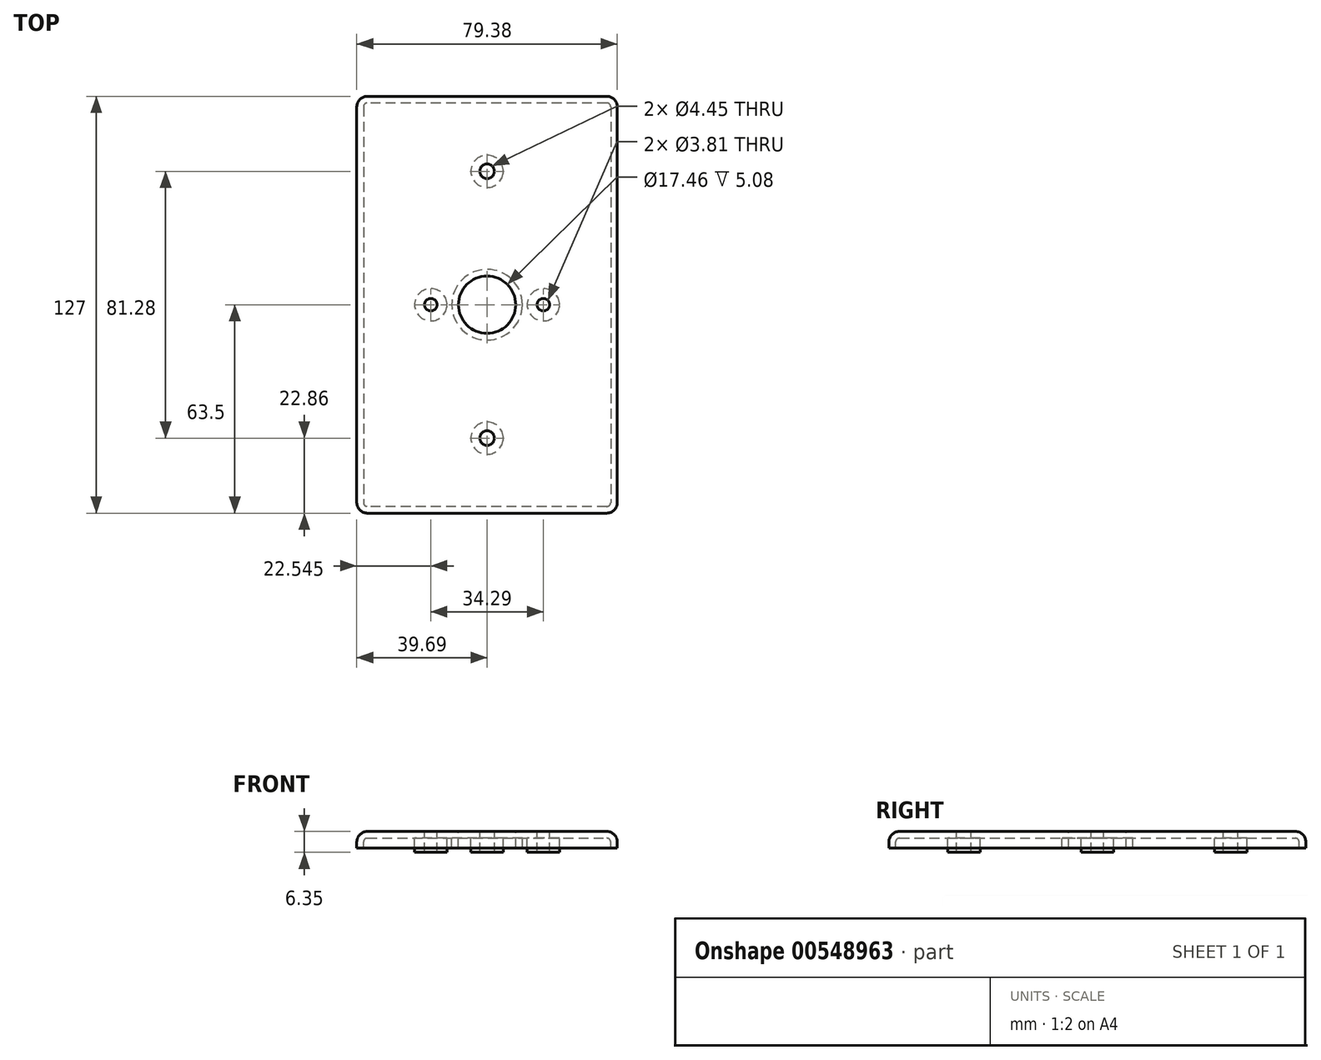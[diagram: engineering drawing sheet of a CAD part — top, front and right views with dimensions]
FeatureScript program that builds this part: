
annotation { "Feature Type Name" : "Feature", "Feature Type Description" : "" }
export const myFeature = defineFeature(function(context is Context, id is Id, definition is map)
    precondition{}
    {
        {
            var Q0;
            Q0=qCreatedBy(makeId("Top.planeOp"),FACE);
            var sketch = newSketch(context, id + "F0", { "sketchPlane" : qUnion([Q0])});
            skLineSegment(sketch, "E0.bottom", {"start": v(36.51, 63.5) * mm, "end": v(-36.51, 63.5) * mm});
            skLineSegment(sketch, "E0.top", {"start": v(36.51, -63.5) * mm, "end": v(-36.51, -63.5) * mm});
            skLineSegment(sketch, "E0.left", {"start": v(39.69, 60.33) * mm, "end": v(39.69, -60.33) * mm});
            skLineSegment(sketch, "E0.right", {"start": v(-39.69, 60.33) * mm, "end": v(-39.69, -60.33) * mm});
            skPoint(sketch, "E0.middle", {"position": v(0, 0) * mm});
            skCircle(sketch, "E1", {"center": v(0, 40.64) * mm, "radius": 2.22 * mm});
            skCircle(sketch, "E2", {"center": v(0, -40.64) * mm, "radius": 2.22 * mm});
            skCircle(sketch, "E3", {"center": v(-17.14, 0) * mm, "radius": 1.9 * mm});
            skCircle(sketch, "E4", {"center": v(17.15, 0) * mm, "radius": 1.9 * mm});
            skPoint(sketch, "E5.visualSharp", {"position": v(-39.69, 63.5) * mm});
            skArc(sketch, "E5.filletArc", {"start": v(-36.51, 63.5) * mm, "mid": v(-38.76, 62.57) * mm, "end": v(-39.69, 60.33) * mm});
            skPoint(sketch, "E6.visualSharp", {"position": v(39.69, 63.5) * mm});
            skArc(sketch, "E6.filletArc", {"start": v(39.69, 60.33) * mm, "mid": v(38.76, 62.57) * mm, "end": v(36.51, 63.5) * mm});
            skPoint(sketch, "E7.visualSharp", {"position": v(39.69, -63.5) * mm});
            skArc(sketch, "E7.filletArc", {"start": v(36.51, -63.5) * mm, "mid": v(38.76, -62.57) * mm, "end": v(39.69, -60.33) * mm});
            skPoint(sketch, "E8.visualSharp", {"position": v(-39.69, -63.5) * mm});
            skArc(sketch, "E8.filletArc", {"start": v(-39.69, -60.33) * mm, "mid": v(-38.76, -62.57) * mm, "end": v(-36.51, -63.5) * mm});
            skCircle(sketch, "E9", {"center": v(0, 0) * mm, "radius": 8.73 * mm});
            skSolve(sketch);
        }
        {
            var Q0;
            Q0=makeQuery(id+"F0.imprint","IMPRINT",FACE,{"disambiguationData":[TD([[makeQuery(id+"F0.imprint","IMPRINT",EDGE,{"derivedFrom":sQuery(id+"F0.wireOp",EDGE,"E0.bottom")}),1.0]])]});
            extrude(context, id + "F1", {"entities" : qUnion([Q0]), "oppositeDirection" : true, "depth" : 5.08 * mm, "offsetDistance" : 25.4 * mm});
        }
        {
            var Q0;
            Q0=makeQuery(id+"F1.opExtrude","CAP_EDGE",EDGE,{"disambiguationData":[OSD([sQuery(id+"F0.wireOp",EDGE,"E0.top")])],"isStart":true});
            fillet(context, id + "F2", {"entities" : qUnion([Q0]), "radius" : 3.17 * mm, "tangentPropagation" : true, "allowEdgeOverflow" : false});
        }
        {
            var Q0;
            Q0=makeQuery(id+"F1.opExtrude","CAP_FACE",FACE,{"disambiguationData":[OSD([sQuery(id+"F0.wireOp",EDGE,"E0.bottom"),sQuery(id+"F0.wireOp",EDGE,"E0.top"),sQuery(id+"F0.wireOp",EDGE,"E0.left"),sQuery(id+"F0.wireOp",EDGE,"E0.right"),sQuery(id+"F0.wireOp",EDGE,"E1"),sQuery(id+"F0.wireOp",EDGE,"E2"),sQuery(id+"F0.wireOp",EDGE,"E3"),sQuery(id+"F0.wireOp",EDGE,"E4"),sQuery(id+"F0.wireOp",EDGE,"E5.filletArc"),sQuery(id+"F0.wireOp",EDGE,"E6.filletArc"),sQuery(id+"F0.wireOp",EDGE,"E7.filletArc"),sQuery(id+"F0.wireOp",EDGE,"E8.filletArc"),sQuery(id+"F0.wireOp",EDGE,"E9")])],"isStart":false});
            shell(context, id + "F3", {"entities" : qUnion([Q0]), "thickness" : 2.03 * mm});
        }
        {
            var Q0;
            Q0=makeQuery(id+"F1.opExtrude","CAP_FACE",FACE,{"disambiguationData":[OSD([sQuery(id+"F0.wireOp",EDGE,"E0.bottom"),sQuery(id+"F0.wireOp",EDGE,"E0.top"),sQuery(id+"F0.wireOp",EDGE,"E0.left"),sQuery(id+"F0.wireOp",EDGE,"E0.right"),sQuery(id+"F0.wireOp",EDGE,"E1"),sQuery(id+"F0.wireOp",EDGE,"E2"),sQuery(id+"F0.wireOp",EDGE,"E3"),sQuery(id+"F0.wireOp",EDGE,"E4"),sQuery(id+"F0.wireOp",EDGE,"E5.filletArc"),sQuery(id+"F0.wireOp",EDGE,"E6.filletArc"),sQuery(id+"F0.wireOp",EDGE,"E7.filletArc"),sQuery(id+"F0.wireOp",EDGE,"E8.filletArc"),sQuery(id+"F0.wireOp",EDGE,"E9")])],"isStart":true});
            var sketch = newSketch(context, id + "F4", { "sketchPlane" : qUnion([Q0])});
            skCircle(sketch, "E10.0", {"center": v(0, 40.64) * mm, "radius": 2.22 * mm});
            skCircle(sketch, "E10.1", {"center": v(17.15, 0) * mm, "radius": 1.9 * mm});
            skCircle(sketch, "E10.2", {"center": v(0, -40.64) * mm, "radius": 2.22 * mm});
            skCircle(sketch, "E10.3", {"center": v(-17.14, 0) * mm, "radius": 1.9 * mm});
            skCircle(sketch, "E11", {"center": v(0, 40.64) * mm, "radius": 4.92 * mm});
            skCircle(sketch, "E12", {"center": v(-17.14, 0) * mm, "radius": 4.92 * mm});
            skCircle(sketch, "E13", {"center": v(17.15, 0) * mm, "radius": 4.92 * mm});
            skCircle(sketch, "E14", {"center": v(0, -40.64) * mm, "radius": 4.92 * mm});
            skSolve(sketch);
        }
        {
            var Q0;
            Q0=makeQuery(id+"F4.imprint","IMPRINT",FACE,{"disambiguationData":[TD([[makeQuery(id+"F4.imprint","IMPRINT",EDGE,{"derivedFrom":sQuery(id+"F4.wireOp",EDGE,"E10.3")}),-1.0]])]});
            var Q1;
            Q1=makeQuery(id+"F4.imprint","IMPRINT",FACE,{"disambiguationData":[TD([[makeQuery(id+"F4.imprint","IMPRINT",EDGE,{"derivedFrom":sQuery(id+"F4.wireOp",EDGE,"E10.1")}),-1.0]])]});
            var Q2;
            Q2=makeQuery(id+"F4.imprint","IMPRINT",FACE,{"disambiguationData":[TD([[makeQuery(id+"F4.imprint","IMPRINT",EDGE,{"derivedFrom":sQuery(id+"F4.wireOp",EDGE,"E10.0")}),-1.0]])]});
            var Q3;
            Q3=makeQuery(id+"F4.imprint","IMPRINT",FACE,{"disambiguationData":[TD([[makeQuery(id+"F4.imprint","IMPRINT",EDGE,{"derivedFrom":sQuery(id+"F4.wireOp",EDGE,"E10.2")}),-1.0]])]});
            extrude(context, id + "F5", {"entities" : qUnion([Q0, Q1, Q2, Q3]), "operationType" : NewBodyOperationType.ADD, "oppositeDirection" : true, "depth" : 6.35 * mm, "offsetDistance" : 25.4 * mm});
        }
    });
